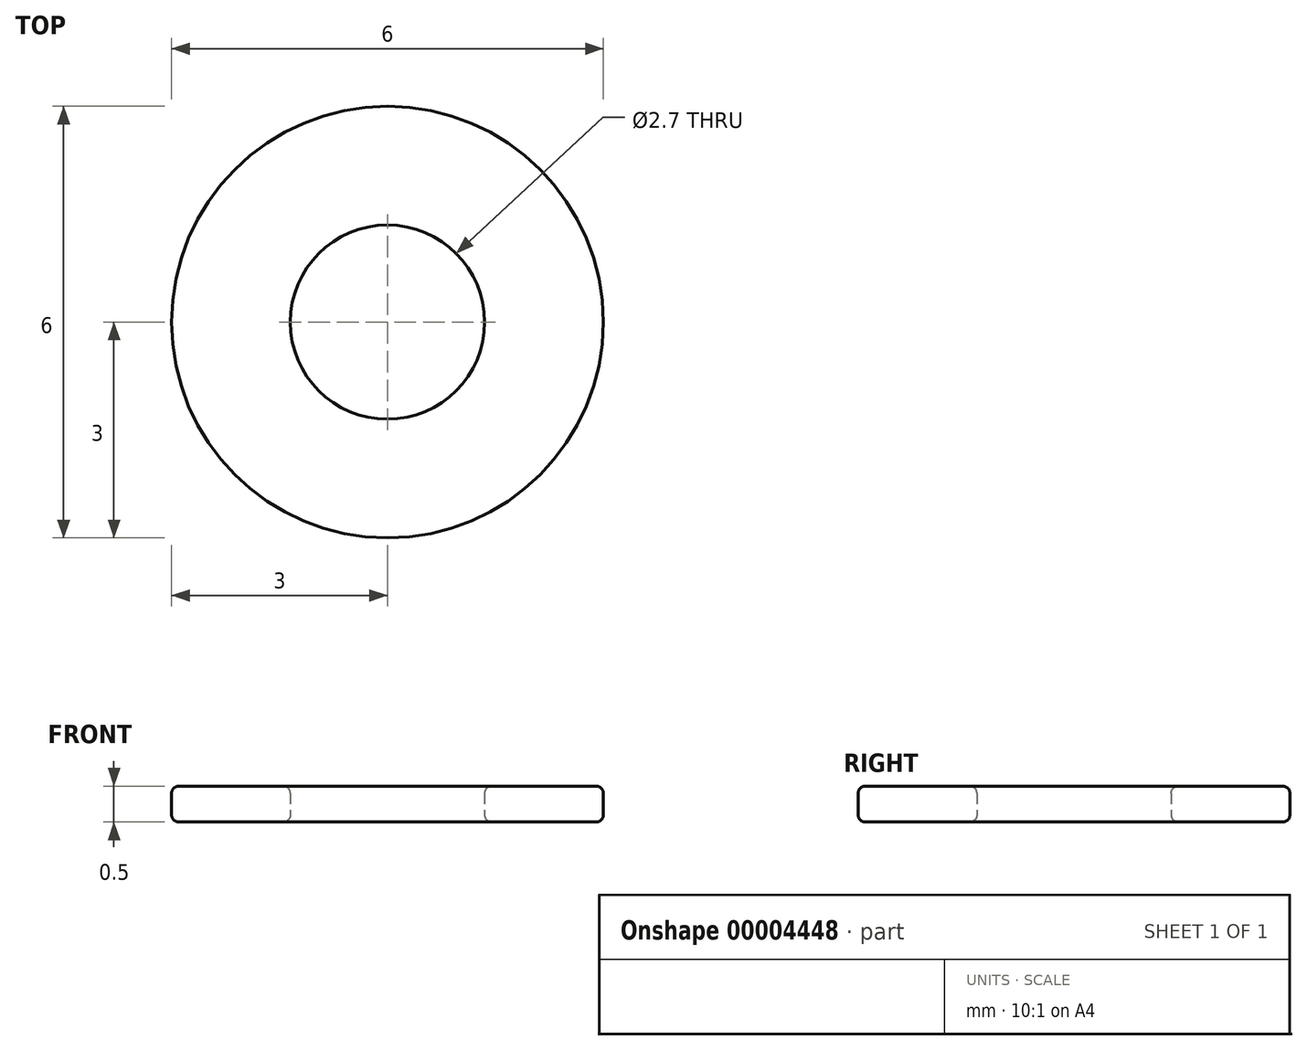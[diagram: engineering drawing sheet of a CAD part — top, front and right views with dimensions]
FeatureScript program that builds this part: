
annotation { "Feature Type Name" : "Feature", "Feature Type Description" : "" }
export const myFeature = defineFeature(function(context is Context, id is Id, definition is map)
    precondition{}
    {
        {
            var Q0;
            Q0=qCreatedBy(makeId("Top.planeOp"),FACE);
            var sketch = newSketch(context, id + "F0", { "sketchPlane" : qUnion([Q0])});
            skCircle(sketch, "E0", {"center": v(0, 0) * mm, "radius": 3 * mm});
            skCircle(sketch, "E1", {"center": v(0, 0) * mm, "radius": 1.35 * mm});
            skSolve(sketch);
        }
        {
            var Q0;
            Q0=makeQuery(id+"F0.imprint","IMPRINT",FACE,{"disambiguationData":[TD([[makeQuery(id+"F0.imprint","IMPRINT",EDGE,{"derivedFrom":sQuery(id+"F0.wireOp",EDGE,"E0")}),1.0]])]});
            extrude(context, id + "F1", {"entities" : qUnion([Q0]), "depth" : .5 * mm});
        }
        {
            var Q0;
            Q0=makeQuery(id+"F1.opExtrude","CAP_FACE",FACE,{"disambiguationData":[OSD([sQuery(id+"F0.wireOp",EDGE,"E0"),sQuery(id+"F0.wireOp",EDGE,"E1")])],"isStart":false});
            var Q1;
            Q1=makeQuery(id+"F1.opExtrude","CAP_FACE",FACE,{"disambiguationData":[OSD([sQuery(id+"F0.wireOp",EDGE,"E0"),sQuery(id+"F0.wireOp",EDGE,"E1")])],"isStart":true});
            fillet(context, id + "F2", {"entities" : qUnion([Q0, Q1]), "radius" : .1 * mm, "tangentPropagation" : true, "allowEdgeOverflow" : false});
        }
    });
